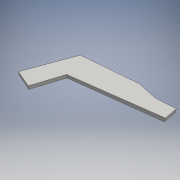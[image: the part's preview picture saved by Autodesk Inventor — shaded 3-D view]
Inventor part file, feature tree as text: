
AUTODESK INVENTOR PART (.ipt)
format: ipt  version: 2016 (Build 200138000, 138)  size: 115,200 bytes
history: native  units: mm
features: extrude x2, sketch x2
ambient origin geometry x8: Origin, YZ Plane, XZ Plane, XY Plane, X Axis, Y Axis, Z Axis, Center Point
bodies: Solid1 (feature_tree)
feature tree (4):
  extrude  "Extrusion1"  Depth=300.0mm
  extrude  "Extrusion2"  Depth=170.0mm
  sketch  "Sketch1"  dims[d0=300.0mm d1=90.0mm]
  sketch  "Sketch2"  dims[d2=70.0mm d3=170.0mm d5=105.0deg d6=0.0mm d7=0.0mm d8=0.0mm d9=300.0mm d10=10.0mm d11=0.0mm d12=40.0mm d13=20.0mm d14=50.0mm d15=140.0mm d16=27.925268mm d17=10.0mm d18=0.0mm]
